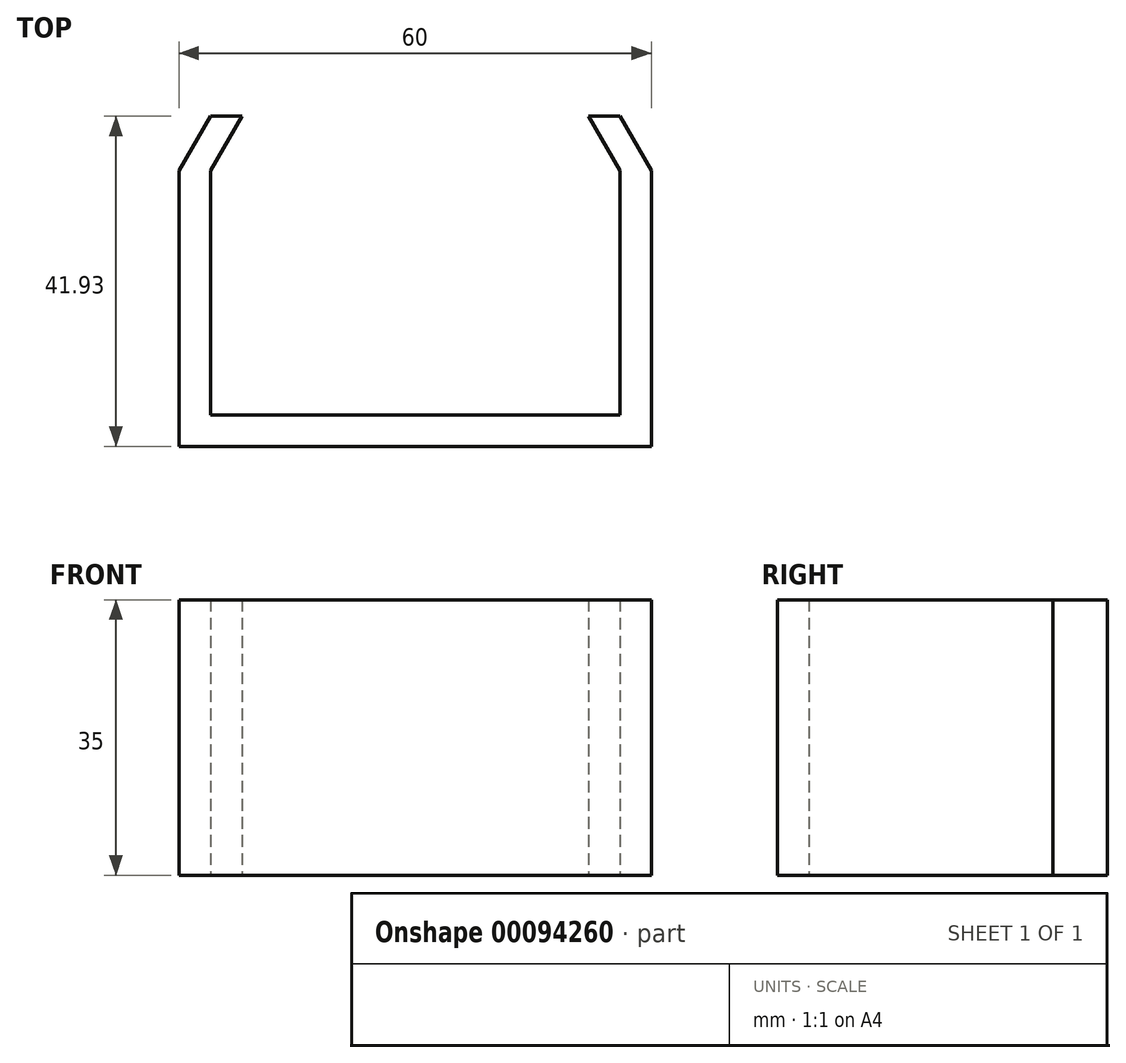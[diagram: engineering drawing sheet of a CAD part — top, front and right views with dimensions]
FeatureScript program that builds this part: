
annotation { "Feature Type Name" : "Feature", "Feature Type Description" : "" }
export const myFeature = defineFeature(function(context is Context, id is Id, definition is map)
    precondition{}
    {
        {
            var Q0;
            Q0=qCreatedBy(makeId("Top.planeOp"),FACE);
            var sketch = newSketch(context, id + "F0", { "sketchPlane" : qUnion([Q0])});
            skLineSegment(sketch, "E0.bottom", {"start": v(0, 0) * mm, "end": v(52, 0) * mm});
            skLineSegment(sketch, "E0.top", {"start": v(0, 31) * mm, "end": v(52, 31) * mm});
            skLineSegment(sketch, "E0.left", {"start": v(0, 0) * mm, "end": v(0, 31) * mm});
            skLineSegment(sketch, "E0.right", {"start": v(52, 0) * mm, "end": v(52, 31) * mm});
            skLineSegment(sketch, "E1.top", {"start": v(0, -4) * mm, "end": v(52, -4) * mm});
            skLineSegment(sketch, "E1.left", {"start": v(0, 0) * mm, "end": v(0, -4) * mm});
            skLineSegment(sketch, "E1.right", {"start": v(52, 0) * mm, "end": v(52, -4) * mm});
            skLineSegment(sketch, "E2.bottom", {"start": v(0, 0) * mm, "end": v(-4, 0) * mm});
            skLineSegment(sketch, "E2.top", {"start": v(0, 31) * mm, "end": v(-4, 31) * mm});
            skLineSegment(sketch, "E2.right", {"start": v(-4, 0) * mm, "end": v(-4, 31) * mm});
            skLineSegment(sketch, "E3.top", {"start": v(0, -4) * mm, "end": v(-4, -4) * mm});
            skLineSegment(sketch, "E3.right", {"start": v(-4, 0) * mm, "end": v(-4, -4) * mm});
            skLineSegment(sketch, "E4.bottom", {"start": v(52, 0) * mm, "end": v(56, 0) * mm});
            skLineSegment(sketch, "E4.top", {"start": v(52, 31) * mm, "end": v(56, 31) * mm});
            skLineSegment(sketch, "E4.right", {"start": v(56, 0) * mm, "end": v(56, 31) * mm});
            skLineSegment(sketch, "E5.top", {"start": v(52, -4) * mm, "end": v(56, -4) * mm});
            skLineSegment(sketch, "E5.right", {"start": v(56, 0) * mm, "end": v(56, -4) * mm});
            skLineSegment(sketch, "E6", {"start": v(-4, 31) * mm, "end": v(0, 37.93) * mm});
            skLineSegment(sketch, "E7", {"start": v(0, 31) * mm, "end": v(4, 37.93) * mm});
            skLineSegment(sketch, "E8", {"start": v(0, 37.93) * mm, "end": v(4, 37.93) * mm});
            skLineSegment(sketch, "E9", {"start": v(56, 31) * mm, "end": v(52, 37.93) * mm});
            skLineSegment(sketch, "E10", {"start": v(52, 31) * mm, "end": v(48, 37.93) * mm});
            skLineSegment(sketch, "E11", {"start": v(52, 37.93) * mm, "end": v(48, 37.93) * mm});
            skLineSegment(sketch, "E12.bottom", {"start": v(0, 0) * mm, "end": v(10, 0) * mm});
            skLineSegment(sketch, "E12.top", {"start": v(0, 8) * mm, "end": v(10, 8) * mm});
            skLineSegment(sketch, "E12.left", {"start": v(0, 0) * mm, "end": v(0, 8) * mm});
            skLineSegment(sketch, "E12.right", {"start": v(10, 0) * mm, "end": v(10, 8) * mm});
            skLineSegment(sketch, "E13.bottom", {"start": v(52, 0) * mm, "end": v(42, 0) * mm});
            skLineSegment(sketch, "E13.top", {"start": v(52, 8) * mm, "end": v(42, 8) * mm});
            skLineSegment(sketch, "E13.left", {"start": v(52, 0) * mm, "end": v(52, 8) * mm});
            skLineSegment(sketch, "E13.right", {"start": v(42, 0) * mm, "end": v(42, 8) * mm});
            skSolve(sketch);
        }
        {
            var Q0;
            Q0=makeQuery(id+"F0.imprint","IMPRINT",FACE,{"disambiguationData":[TD([[makeQuery(id+"F0.imprint","IMPRINT",EDGE,{"derivedFrom":sQuery(id+"F0.wireOp",EDGE,"E2.top")}),-1.0]])]});
            var Q1;
            Q1=makeQuery(id+"F0.imprint","IMPRINT",FACE,{"disambiguationData":[TD([[makeQuery(id+"F0.imprint","IMPRINT",EDGE,{"derivedFrom":sQuery(id+"F0.wireOp",EDGE,"E2.top")}),1.0]])]});
            var Q2;
            Q2=makeQuery(id+"F0.imprint","IMPRINT",FACE,{"disambiguationData":[TD([[makeQuery(id+"F0.imprint","IMPRINT",EDGE,{"derivedFrom":sQuery(id+"F0.wireOp",EDGE,"E2.bottom")}),1.0]])]});
            var Q3;
            Q3=makeQuery(id+"F0.imprint","IMPRINT",FACE,{"disambiguationData":[TD([[makeQuery(id+"F0.imprint","IMPRINT",EDGE,{"derivedFrom":sQuery(id+"F0.wireOp",EDGE,"E0.bottom")}),-1.0]])]});
            var Q4;
            Q4=makeQuery(id+"F0.imprint","IMPRINT",FACE,{"disambiguationData":[TD([[makeQuery(id+"F0.imprint","IMPRINT",EDGE,{"derivedFrom":sQuery(id+"F0.wireOp",EDGE,"E4.bottom")}),-1.0]])]});
            var Q5;
            Q5=makeQuery(id+"F0.imprint","IMPRINT",FACE,{"disambiguationData":[TD([[makeQuery(id+"F0.imprint","IMPRINT",EDGE,{"derivedFrom":sQuery(id+"F0.wireOp",EDGE,"E4.top")}),-1.0]])]});
            var Q6;
            Q6=makeQuery(id+"F0.imprint","IMPRINT",FACE,{"disambiguationData":[TD([[makeQuery(id+"F0.imprint","IMPRINT",EDGE,{"derivedFrom":sQuery(id+"F0.wireOp",EDGE,"E4.top")}),1.0]])]});
            var Q7;
            Q7=makeQuery(id+"F0.imprint","IMPRINT",FACE,{"disambiguationData":[TD([[makeQuery(id+"F0.imprint","IMPRINT",EDGE,{"derivedFrom":sQuery(id+"F0.wireOp",EDGE,"E12.bottom")}),1.0]])]});
            var Q8;
            Q8=makeQuery(id+"F0.imprint","IMPRINT",FACE,{"disambiguationData":[TD([[makeQuery(id+"F0.imprint","IMPRINT",EDGE,{"derivedFrom":sQuery(id+"F0.wireOp",EDGE,"E13.bottom")}),-1.0]])]});
            extrude(context, id + "F1", {"entities" : qUnion([Q0, Q1, Q2, Q3, Q4, Q5, Q6, Q7, Q8]), "depth" : 35 * mm});
        }
    });
